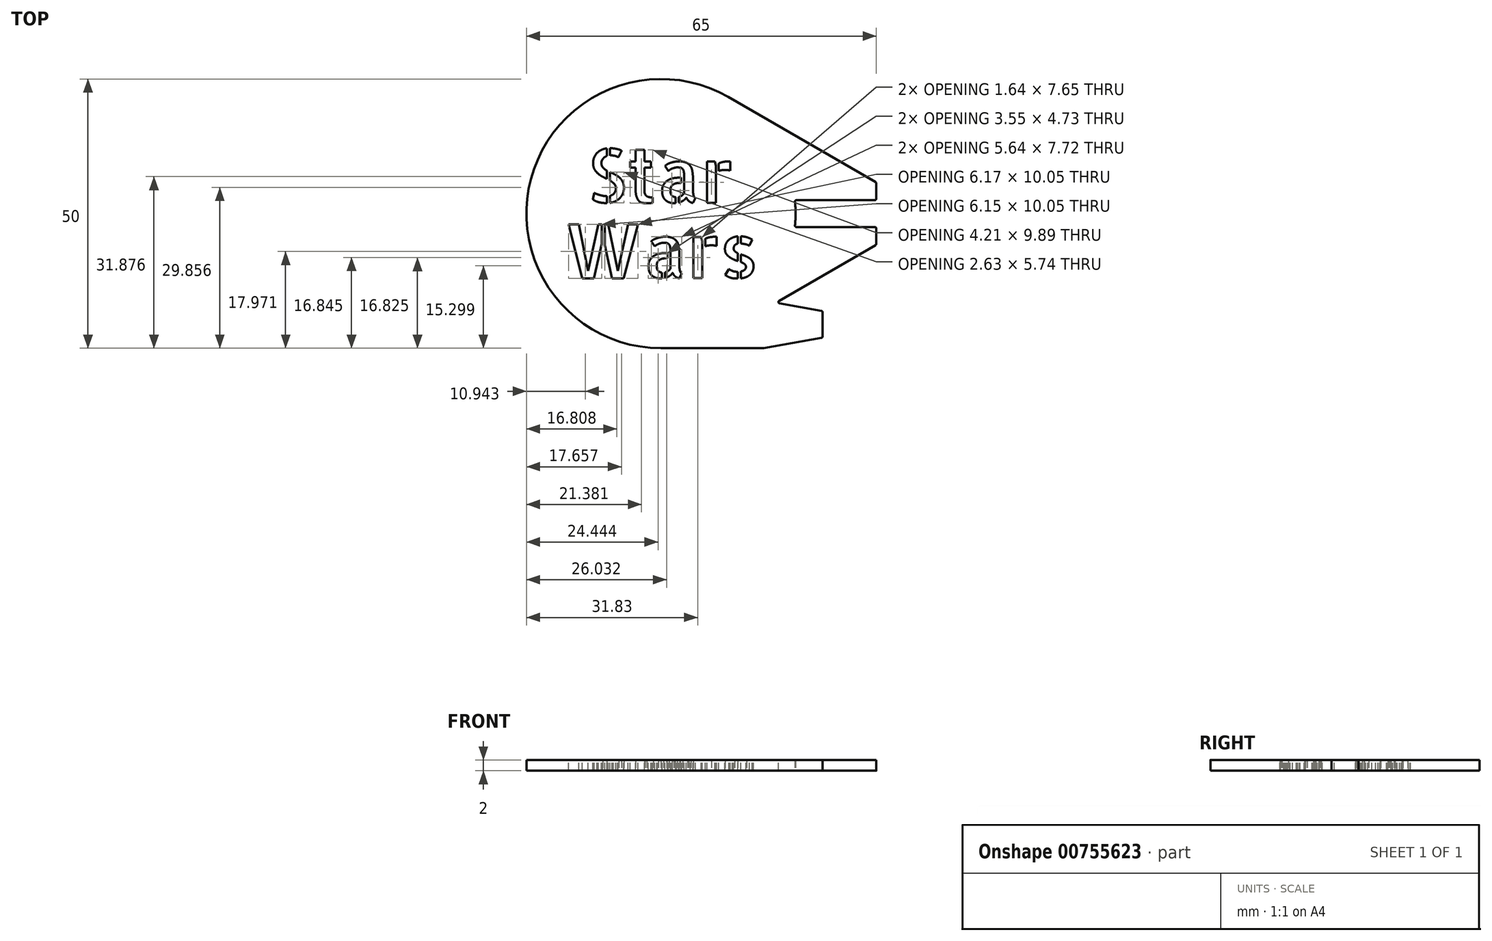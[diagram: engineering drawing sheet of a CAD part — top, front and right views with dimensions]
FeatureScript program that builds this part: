
annotation { "Feature Type Name" : "Feature", "Feature Type Description" : "" }
export const myFeature = defineFeature(function(context is Context, id is Id, definition is map)
    precondition{}
    {
        {
            var Q0;
            Q0=qCreatedBy(makeId("Top.planeOp"),FACE);
            var sketch = newSketch(context, id + "F0", { "sketchPlane" : qUnion([Q0])});
            skCircle(sketch, "E0", {"center": v(0, 0) * mm, "radius": 25 * mm});
            skLineSegment(sketch, "E1", {"start": v(24.87, 2.5) * mm, "end": v(40, 2.5) * mm});
            skLineSegment(sketch, "E2", {"start": v(40, 2.5) * mm, "end": v(40, 5.77) * mm});
            skLineSegment(sketch, "E3", {"start": v(40, 5.77) * mm, "end": v(12.5, 21.65) * mm});
            skLineSegment(sketch, "E4", {"start": v(0, 0) * mm, "end": v(25, 0) * mm, "construction": true});
            skLineSegment(sketch, "E5.MirrorCS", {"start": v(40, -5.77) * mm, "end": v(12.5, -21.65) * mm});
            skLineSegment(sketch, "E6.MirrorCS", {"start": v(40, -2.5) * mm, "end": v(40, -5.77) * mm});
            skLineSegment(sketch, "E7.MirrorCS", {"start": v(24.87, -2.5) * mm, "end": v(40, -2.5) * mm});
            skLineSegment(sketch, "E8", {"start": v(19.08, -16.15) * mm, "end": v(30, -18.08) * mm});
            skLineSegment(sketch, "E9", {"start": v(30, -18.08) * mm, "end": v(30, -23.08) * mm});
            skLineSegment(sketch, "E10", {"start": v(30, -23.08) * mm, "end": v(19.08, -25) * mm});
            skLineSegment(sketch, "E11", {"start": v(19.08, -25) * mm, "end": v(0, -25) * mm});
            skPoint(sketch, "E12", {"position": v(32.44, -2.5) * mm});
            skSolve(sketch);
        }
        {
            var Q0;
            {var subQ0=sQuery(id+"F0.wireOp",EDGE,"E0");var subQ5=makeQuery(id+"F0.imprint","INTERSECT",VERTEX,{"derivedFrom":[subQ0,sQuery(id+"F0.wireOp",EDGE,"E1")]});Q0=makeQuery(id+"F0.imprint","IMPRINT",FACE,{"disambiguationData":[TD([[makeQuery(id+"F0.imprint","IMPRINT",EDGE,{"disambiguationData":[TD([[subQ5,-1.0]])],"derivedFrom":subQ0}),1.0]])]});}
            var Q1;
            {var subQ1=sQuery(id+"F0.wireOp",EDGE,"E6.MirrorCS");Q1=makeQuery(id+"F0.imprint","IMPRINT",FACE,{"disambiguationData":[TD([[makeQuery(id+"F0.imprint","IMPRINT",EDGE,{"derivedFrom":subQ1}),-1.0]])]});}
            var Q2;
            {var subQ0=sQuery(id+"F0.wireOp",EDGE,"E1");Q2=makeQuery(id+"F0.imprint","IMPRINT",FACE,{"disambiguationData":[TD([[makeQuery(id+"F0.imprint","IMPRINT",EDGE,{"derivedFrom":subQ0}),1.0]])]});}
            var Q3;
            {var subQ0=sQuery(id+"F0.wireOp",EDGE,"E9");Q3=makeQuery(id+"F0.imprint","IMPRINT",FACE,{"disambiguationData":[TD([[makeQuery(id+"F0.imprint","IMPRINT",EDGE,{"derivedFrom":subQ0}),-1.0]])]});}
            var Q4;
            {var subQ0=sQuery(id+"F0.wireOp",EDGE,"E5.MirrorCS");var subQ1=sQuery(id+"F0.wireOp",EDGE,"E0");var subQ2=makeQuery(id+"F0.imprint","INTERSECT",VERTEX,{"derivedFrom":[subQ1,subQ0]});Q4=makeQuery(id+"F0.imprint","IMPRINT",FACE,{"disambiguationData":[TD([[makeQuery(id+"F0.imprint","IMPRINT",EDGE,{"disambiguationData":[TD([[subQ2,-1.0]])],"derivedFrom":subQ1}),-1.0]])]});}
            extrude(context, id + "F1", {"entities" : qUnion([Q0, Q1, Q2, Q3, Q4]), "endBound" : BoundingType.SYMMETRIC, "depth" : 2 * mm, "offsetDistance" : 25 * mm});
        }
        {
            var Q0;
            Q0=makeQuery(id+"F1.opExtrude","SWEPT_EDGE",EDGE,{"disambiguationData":[OSD([sQuery(id+"F0.wireOp",EDGE,"E0"),sQuery(id+"F0.wireOp",EDGE,"E11")])]});
            var Q1;
            Q1=makeQuery(id+"F1.opExtrude","SWEPT_EDGE",EDGE,{"disambiguationData":[OSD([sQuery(id+"F0.wireOp",EDGE,"E10"),sQuery(id+"F0.wireOp",EDGE,"E11")])]});
            var Q2;
            Q2=makeQuery(id+"F1.opExtrude","SWEPT_EDGE",EDGE,{"disambiguationData":[OSD([sQuery(id+"F0.wireOp",EDGE,"E9"),sQuery(id+"F0.wireOp",EDGE,"E10")])]});
            var Q3;
            Q3=makeQuery(id+"F1.opExtrude","SWEPT_EDGE",EDGE,{"disambiguationData":[OSD([sQuery(id+"F0.wireOp",EDGE,"E8"),sQuery(id+"F0.wireOp",EDGE,"E9")])]});
            var Q4;
            Q4=makeQuery(id+"F1.opExtrude","SWEPT_EDGE",EDGE,{"disambiguationData":[OSD([sQuery(id+"F0.wireOp",EDGE,"E5.MirrorCS"),sQuery(id+"F0.wireOp",EDGE,"E6.MirrorCS")])]});
            var Q5;
            Q5=makeQuery(id+"F1.opExtrude","SWEPT_EDGE",EDGE,{"disambiguationData":[OSD([sQuery(id+"F0.wireOp",EDGE,"E6.MirrorCS"),sQuery(id+"F0.wireOp",EDGE,"E7.MirrorCS")])]});
            var Q6;
            Q6=makeQuery(id+"F1.opExtrude","SWEPT_EDGE",EDGE,{"disambiguationData":[OSD([sQuery(id+"F0.wireOp",EDGE,"E1"),sQuery(id+"F0.wireOp",EDGE,"E2")])]});
            var Q7;
            Q7=makeQuery(id+"F1.opExtrude","SWEPT_EDGE",EDGE,{"disambiguationData":[OSD([sQuery(id+"F0.wireOp",EDGE,"E2"),sQuery(id+"F0.wireOp",EDGE,"E3")])]});
            var Q8;
            Q8=makeQuery(id+"F1.opExtrude","SWEPT_EDGE",EDGE,{"disambiguationData":[OSD([sQuery(id+"F0.wireOp",EDGE,"E0"),sQuery(id+"F0.wireOp",EDGE,"E1")])]});
            var Q9;
            Q9=makeQuery(id+"F1.opExtrude","SWEPT_EDGE",EDGE,{"disambiguationData":[OSD([sQuery(id+"F0.wireOp",EDGE,"E5.MirrorCS"),sQuery(id+"F0.wireOp",EDGE,"E8")])]});
            var Q10;
            Q10=makeQuery(id+"F1.opExtrude","SWEPT_EDGE",EDGE,{"disambiguationData":[OSD([sQuery(id+"F0.wireOp",EDGE,"E0"),sQuery(id+"F0.wireOp",EDGE,"E7.MirrorCS")])]});
            var Q11;
            Q11=makeQuery(id+"F1.opExtrude","SWEPT_EDGE",EDGE,{"disambiguationData":[OSD([sQuery(id+"F0.wireOp",EDGE,"E0"),sQuery(id+"F0.wireOp",EDGE,"E3")])]});
            fillet(context, id + "F2", {"entities" : qUnion([Q0, Q1, Q2, Q3, Q4, Q5, Q6, Q7, Q8, Q9, Q10, Q11]), "radius" : 0.25 * mm, "tangentPropagation" : true, "allowEdgeOverflow" : false});
        }
        {
            var Q0;
            Q0=makeQuery(id+"F1.opExtrude","CAP_FACE",FACE,{"disambiguationData":[OSD([sQuery(id+"F0.wireOp",EDGE,"E0"),sQuery(id+"F0.wireOp",EDGE,"E1"),sQuery(id+"F0.wireOp",EDGE,"E2"),sQuery(id+"F0.wireOp",EDGE,"E3"),sQuery(id+"F0.wireOp",EDGE,"E5.MirrorCS"),sQuery(id+"F0.wireOp",EDGE,"E6.MirrorCS"),sQuery(id+"F0.wireOp",EDGE,"E7.MirrorCS"),sQuery(id+"F0.wireOp",EDGE,"E8"),sQuery(id+"F0.wireOp",EDGE,"E9"),sQuery(id+"F0.wireOp",EDGE,"E10"),sQuery(id+"F0.wireOp",EDGE,"E11")])],"isStart":false});
            var sketch = newSketch(context, id + "F3", { "sketchPlane" : qUnion([Q0])});
            skText(sketch, "E13", { "text": "Star", "fontName": "AllertaStencil-Regular.ttf"});
            skText(sketch, "E14", { "text": "Wars", "fontName": "AllertaStencil-Regular.ttf"});
            skLineSegment(sketch, "E15", {"start": v(0, -2) * mm, "end": v(0, 2) * mm});
            skPoint(sketch, "E16", {"position": v(0, 0) * mm});
            const initialGuessF3  = {"E13": [-0.01378, 0.002, 1, 0, 0.01], "E14": [-0.01812, -0.012, 1, 0, 0.01]};
            skSetInitialGuess(sketch, initialGuessF3);
            skSolve(sketch);
        }
        {
            var Q0;
            Q0 = qSketchRegion(id + "F3", true);
            extrude(context, id + "F4", {"entities" : qUnion([Q0]), "operationType" : NewBodyOperationType.REMOVE, "endBound" : BoundingType.UP_TO_NEXT, "oppositeDirection" : true, "depth" : 1 * mm, "offsetDistance" : 25 * mm});
        }
    });
